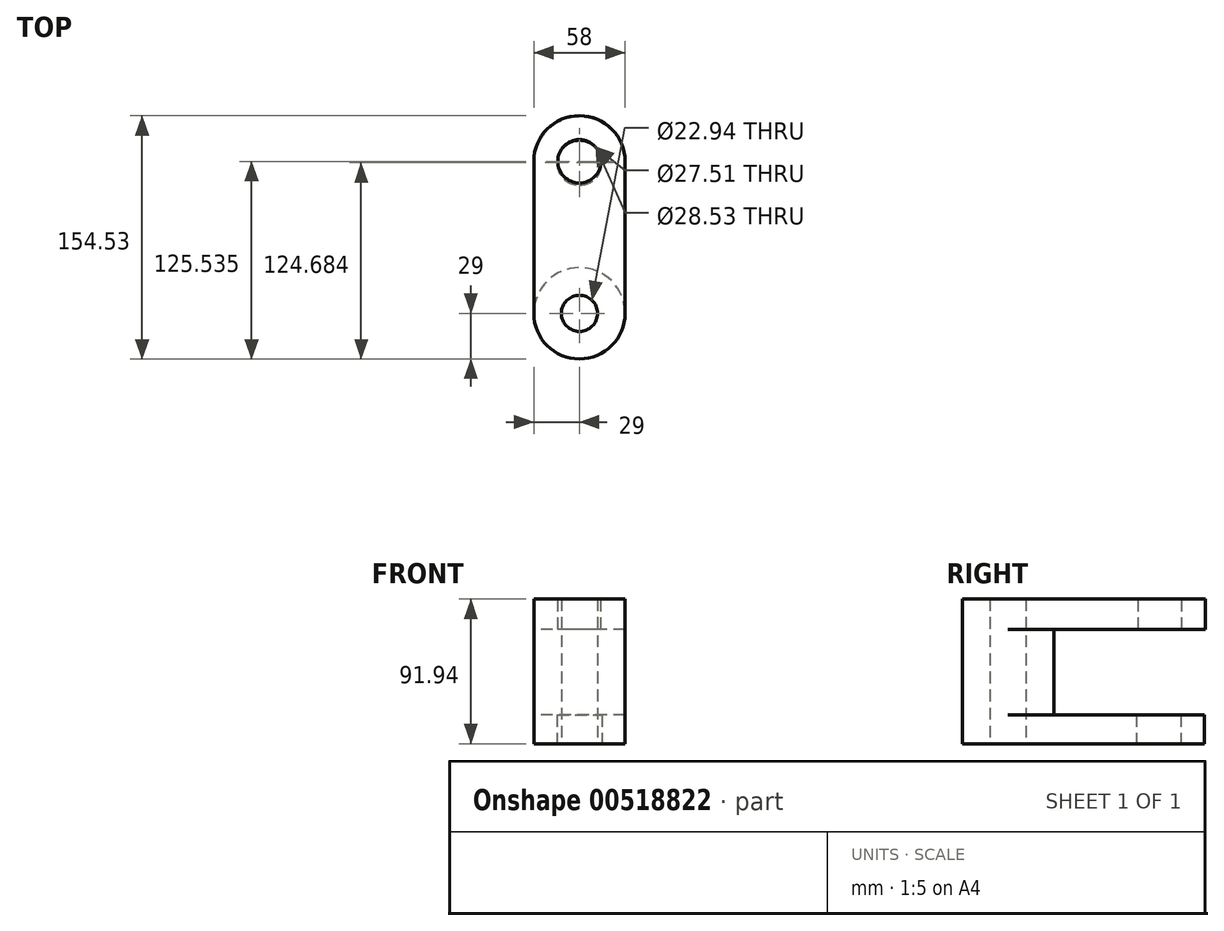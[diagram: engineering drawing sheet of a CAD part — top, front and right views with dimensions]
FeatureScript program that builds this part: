
annotation { "Feature Type Name" : "Feature", "Feature Type Description" : "" }
export const myFeature = defineFeature(function(context is Context, id is Id, definition is map)
    precondition{}
    {
        {
            var Q0;
            Q0=qCreatedBy(makeId("Top.planeOp"),FACE);
            var sketch = newSketch(context, id + "F0", { "sketchPlane" : qUnion([Q0])});
            skCircle(sketch, "E0", {"center": v(0, 0) * mm, "radius": 29 * mm});
            skCircle(sketch, "E1.0", {"center": v(0, 0) * mm, "radius": 11.47 * mm});
            skSolve(sketch);
        }
        {
            var Q0;
            Q0 = qSketchRegion(id + "F0", true);
            extrude(context, id + "F1", {"entities" : qUnion([Q0]), "endBound" : BoundingType.SYMMETRIC, "depth" : 91.95 * mm, "offsetDistance" : 25.4 * mm});
        }
        {
            var Q0;
            Q0=makeQuery(id+"F1.opExtrude","CAP_FACE",FACE,{"disambiguationData":[OSD([sQuery(id+"F0.wireOp",EDGE,"E0"),sQuery(id+"F0.wireOp",EDGE,"E1.0")])],"isStart":false});
            var sketch = newSketch(context, id + "F2", { "sketchPlane" : qUnion([Q0])});
            skLineSegment(sketch, "E2", {"start": v(-29, 0) * mm, "end": v(-29, 96.54) * mm});
            skLineSegment(sketch, "E3", {"start": v(29, 0) * mm, "end": v(29, 96.54) * mm});
            skArc(sketch, "E4", {"start": v(29, 96.54) * mm, "mid": v(0, 125.53) * mm, "end": v(-29, 96.54) * mm});
            skArc(sketch, "E5", {"start": v(-29, 96.54) * mm, "mid": v(0, 67.54) * mm, "end": v(29, 96.54) * mm});
            skArc(sketch, "E6.0", {"start": v(13.76, 96.54) * mm, "mid": v(0, 110.3) * mm, "end": v(-13.76, 96.54) * mm});
            skArc(sketch, "E7.0", {"start": v(-13.76, 96.54) * mm, "mid": v(0, 82.78) * mm, "end": v(13.76, 96.54) * mm});
            skSolve(sketch);
        }
        {
            var Q0;
            Q0 = qSketchRegion(id + "F2", true);
            var Q1;
            {var subQ0=sQuery(id+"F2.wireOp",EDGE,"E2");Q1=makeQuery(id+"F2.imprint","IMPRINT",FACE,{"disambiguationData":[TD([[makeQuery(id+"F2.imprint","IMPRINT",EDGE,{"derivedFrom":subQ0}),-1.0]])]});}
            extrude(context, id + "F3", {"entities" : qUnion([Q0, Q1]), "operationType" : NewBodyOperationType.ADD, "oppositeDirection" : true, "depth" : 19.3 * mm, "offsetDistance" : 25.4 * mm});
        }
        {
            var Q0;
            Q0=makeQuery(id+"F1.opExtrude","CAP_FACE",FACE,{"disambiguationData":[OSD([sQuery(id+"F0.wireOp",EDGE,"E0"),sQuery(id+"F0.wireOp",EDGE,"E1.0")])],"isStart":true});
            var sketch = newSketch(context, id + "F4", { "sketchPlane" : qUnion([Q0])});
            skLineSegment(sketch, "E8", {"start": v(29, 0) * mm, "end": v(29, -95.68) * mm});
            skLineSegment(sketch, "E9", {"start": v(-29, 0) * mm, "end": v(-29, -95.68) * mm});
            skArc(sketch, "E10", {"start": v(-29, -95.68) * mm, "mid": v(0, -124.68) * mm, "end": v(29, -95.68) * mm});
            skArc(sketch, "E11", {"start": v(29, -95.68) * mm, "mid": v(0, -66.69) * mm, "end": v(-29, -95.68) * mm});
            skArc(sketch, "E12.0", {"start": v(-14.26, -95.68) * mm, "mid": v(0, -109.95) * mm, "end": v(14.26, -95.68) * mm});
            skArc(sketch, "E12.1", {"start": v(14.26, -95.68) * mm, "mid": v(0, -81.42) * mm, "end": v(-14.26, -95.68) * mm});
            skSolve(sketch);
        }
        {
            var Q0;
            {var subQ0=sQuery(id+"F4.wireOp",EDGE,"E8");Q0=makeQuery(id+"F4.imprint","IMPRINT",FACE,{"disambiguationData":[TD([[makeQuery(id+"F4.imprint","IMPRINT",EDGE,{"derivedFrom":subQ0}),-1.0]])]});}
            var Q1;
            Q1=makeQuery(id+"F4.imprint","IMPRINT",FACE,{"disambiguationData":[TD([[makeQuery(id+"F4.imprint","IMPRINT",EDGE,{"derivedFrom":sQuery(id+"F4.wireOp",EDGE,"E10")}),1.0]])]});
            extrude(context, id + "F5", {"entities" : qUnion([Q0, Q1]), "operationType" : NewBodyOperationType.ADD, "oppositeDirection" : true, "depth" : 18.29 * mm, "offsetDistance" : 25.4 * mm});
        }
    });
